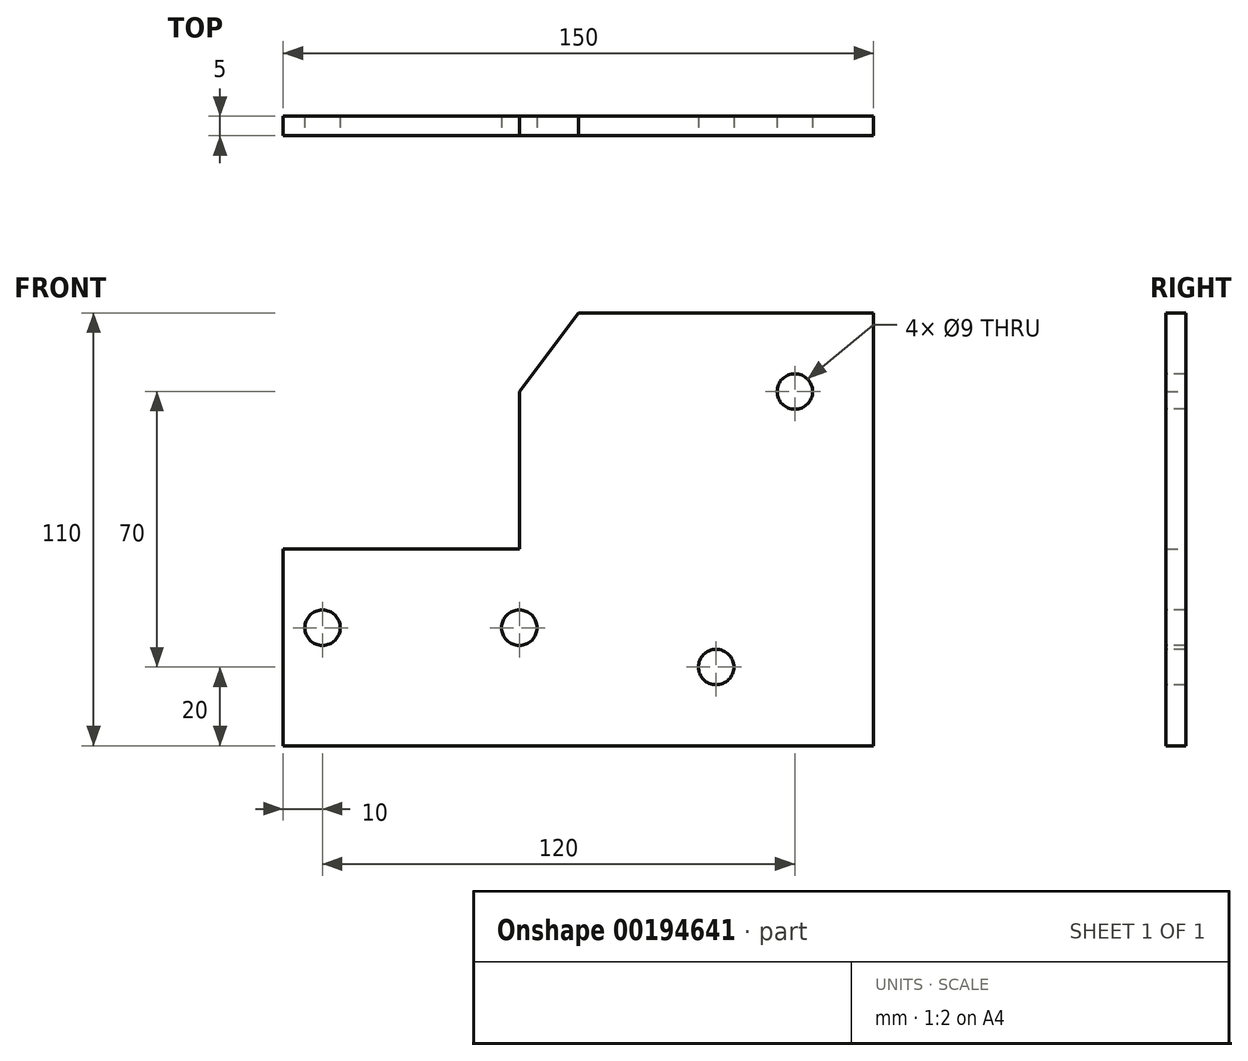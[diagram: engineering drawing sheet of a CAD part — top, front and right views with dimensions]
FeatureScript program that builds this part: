
annotation { "Feature Type Name" : "Feature", "Feature Type Description" : "" }
export const myFeature = defineFeature(function(context is Context, id is Id, definition is map)
    precondition{}
    {
        {
            var Q0;
            Q0=qCreatedBy(makeId("Front.planeOp"),FACE);
            var sketch = newSketch(context, id + "F0", { "sketchPlane" : qUnion([Q0])});
            skLineSegment(sketch, "E0", {"start": v(0, 0) * mm, "end": v(0, 50) * mm});
            skLineSegment(sketch, "E1", {"start": v(0, 50) * mm, "end": v(60, 50) * mm});
            skLineSegment(sketch, "E2", {"start": v(60, 50) * mm, "end": v(60, 90) * mm});
            skLineSegment(sketch, "E3", {"start": v(60, 90) * mm, "end": v(75, 110) * mm});
            skLineSegment(sketch, "E4", {"start": v(75, 110) * mm, "end": v(150, 110) * mm});
            skLineSegment(sketch, "E5", {"start": v(150, 110) * mm, "end": v(150, 0) * mm});
            skLineSegment(sketch, "E6", {"start": v(150, 0) * mm, "end": v(0, 0) * mm});
            skSolve(sketch);
        }
        {
            var Q0;
            Q0 = qSketchRegion(id + "F0", true);
            extrude(context, id + "F1", {"entities" : qUnion([Q0]), "depth" : 5 * mm});
        }
        {
            var Q0;
            Q0=makeQuery(id+"F1.opExtrude","CAP_FACE",FACE,{"disambiguationData":[OSD([sQuery(id+"F0.wireOp",EDGE,"E0"),sQuery(id+"F0.wireOp",EDGE,"E1"),sQuery(id+"F0.wireOp",EDGE,"E2"),sQuery(id+"F0.wireOp",EDGE,"E3"),sQuery(id+"F0.wireOp",EDGE,"E4"),sQuery(id+"F0.wireOp",EDGE,"E5"),sQuery(id+"F0.wireOp",EDGE,"E6")])],"isStart":false});
            var sketch = newSketch(context, id + "F2", { "sketchPlane" : qUnion([Q0])});
            skPoint(sketch, "E7", {"position": v(10, 30) * mm});
            skPoint(sketch, "E8", {"position": v(60, 30) * mm});
            skSolve(sketch);
        }
        {
            var Q0;
            Q0=sQuery(id+"F2.wireOp",VERTEX,"E7");
            var Q1;
            Q1=sQuery(id+"F2.wireOp",VERTEX,"E8");
            var Q2;
            Q2=makeQuery(id+"F1.opExtrude","SWEPT_BODY",BODY,{"disambiguationData":[OSD([sQuery(id+"F0.wireOp",EDGE,"E0"),sQuery(id+"F0.wireOp",EDGE,"E1"),sQuery(id+"F0.wireOp",EDGE,"E2"),sQuery(id+"F0.wireOp",EDGE,"E3"),sQuery(id+"F0.wireOp",EDGE,"E4"),sQuery(id+"F0.wireOp",EDGE,"E5"),sQuery(id+"F0.wireOp",EDGE,"E6")])]});
            hole(context, id + "F3", {"style" : HoleStyle.SIMPLE, "endStyle" : HoleEndStyle.THROUGH, "holeDiameter" : 9 * mm, "startFromSketch" : true, "locations" : qUnion([Q0, Q1]), "scope" : qUnion([Q2]), "isTappedThrough" : true});
        }
        {
            var Q0;
            Q0=makeQuery(id+"F1.opExtrude","CAP_FACE",FACE,{"disambiguationData":[OSD([sQuery(id+"F0.wireOp",EDGE,"E0"),sQuery(id+"F0.wireOp",EDGE,"E1"),sQuery(id+"F0.wireOp",EDGE,"E2"),sQuery(id+"F0.wireOp",EDGE,"E3"),sQuery(id+"F0.wireOp",EDGE,"E4"),sQuery(id+"F0.wireOp",EDGE,"E5"),sQuery(id+"F0.wireOp",EDGE,"E6")])],"isStart":false});
            var sketch = newSketch(context, id + "F4", { "sketchPlane" : qUnion([Q0])});
            skPoint(sketch, "E9", {"position": v(110, 20) * mm});
            skPoint(sketch, "E10", {"position": v(130, 90) * mm});
            skSolve(sketch);
        }
        {
            var Q0;
            Q0=sQuery(id+"F4.wireOp",VERTEX,"E9");
            var Q1;
            Q1=sQuery(id+"F4.wireOp",VERTEX,"E10");
            var Q2;
            Q2=makeQuery(id+"F1.opExtrude","SWEPT_BODY",BODY,{"disambiguationData":[OSD([sQuery(id+"F0.wireOp",EDGE,"E0"),sQuery(id+"F0.wireOp",EDGE,"E1"),sQuery(id+"F0.wireOp",EDGE,"E2"),sQuery(id+"F0.wireOp",EDGE,"E3"),sQuery(id+"F0.wireOp",EDGE,"E4"),sQuery(id+"F0.wireOp",EDGE,"E5"),sQuery(id+"F0.wireOp",EDGE,"E6")])]});
            hole(context, id + "F5", {"style" : HoleStyle.SIMPLE, "endStyle" : HoleEndStyle.THROUGH, "holeDiameter" : 9 * mm, "startFromSketch" : true, "locations" : qUnion([Q0, Q1]), "scope" : qUnion([Q2]), "isTappedThrough" : true});
        }
    });
